FCSTD DOCUMENT  (FreeCAD 0.19R0.19.2)
Label: waferHolder_001
License: All rights reserved
LicenseURL: http://en.wikipedia.org/wiki/All_rights_reserved
objects: Sketcher::SketchObject×1
note: 1 computed .brp shape members not serialized (recipe doc carries the construction recipe); baked Part::Feature solids carry a one-line shape summary decoded from their .brp

FEATURE [Sketcher::SketchObject] Sketch
  FullyConstrained = true
  sketch-geometry (14):
    g0: Circle CenterX=-3.1415e-12 CenterY=5.6243e-12 CenterZ=0 NormalX=0 NormalY=0 NormalZ=1 AngleXU=0 Radius=63
    g1: ArcOfCircle CenterX=-3.1415e-12 CenterY=5.6243e-12 CenterZ=0 NormalX=0 NormalY=0 NormalZ=1 AngleXU=0 Radius=74.8482 StartAngle=5.07429 EndAngle=10.6337
    g2: LineSegment StartX=-26.5 StartY=-70.0001 StartZ=0 EndX=26.5 EndY=-70.0001 EndZ=0
    g3: LineSegment StartX=-79 StartY=-4 StartZ=0 EndX=-75 EndY=-4 EndZ=0
    g4: LineSegment StartX=-79 StartY=-4 StartZ=0 EndX=-79 EndY=4 EndZ=0
    g5: LineSegment StartX=-79 StartY=4 StartZ=0 EndX=-71 EndY=4 EndZ=0
    g6: LineSegment StartX=-71 StartY=4 StartZ=0 EndX=-71 EndY=-4 EndZ=0
    g7: LineSegment StartX=-75 StartY=-4 StartZ=0 EndX=-71 EndY=-4 EndZ=0
    g8: LineSegment StartX=-75 StartY=5.6235e-12 StartZ=0 EndX=-75 EndY=-4 EndZ=0
    g9: LineSegment StartX=71 StartY=-4 StartZ=0 EndX=75 EndY=-4 EndZ=0
    g10: LineSegment StartX=71 StartY=-4 StartZ=0 EndX=71 EndY=4 EndZ=0
    g11: LineSegment StartX=71 StartY=4 StartZ=0 EndX=79 EndY=4 EndZ=0
    g12: LineSegment StartX=79 StartY=4 StartZ=0 EndX=79 EndY=-4 EndZ=0
    g13: LineSegment StartX=75 StartY=-4 StartZ=0 EndX=79 EndY=-4 EndZ=0
  constraints (39):
    c: Block(g0)
    c: Coincident(g1,g0)
    c: Block(g1)
    c: Coincident(g2,g1)
    c: Coincident(g2,g1)
    c: Horizontal(g2)
    c: Horizontal(g3)
    c: Distance(g3) = 4
    c: Vertical(g4)
    c: Distance(g4) = 8
    c: Coincident(g4,g3)
    c: Horizontal(g5)
    c: Distance(g5) = 8
    c: Coincident(g5,g4)
    c: Vertical(g6)
    c: Distance(g6) = 8
    c: Coincident(g6,g5)
    c: Coincident(g7,g6)
    c: Horizontal(g7)
    c: Vertical(g8)
    c: Distance(g8) = 4
    c: Block(g5)
    c: Coincident(g8,g3)
    c: Block(g7)
    c: Horizontal(g9)
    c: Equal(g3,g9) = 4
    c: Vertical(g10)
    c: Equal(g4,g10) = 8
    c: Coincident(g10,g9)
    c: Horizontal(g11)
    c: Equal(g5,g11) = 8
    c: Coincident(g11,g10)
    c: Vertical(g12)
    c: Equal(g6,g12) = 8
    c: Coincident(g12,g11)
    c: Coincident(g13,g12)
    c: Horizontal(g13)
    c: Block(g11)
    c: Block(g13)
